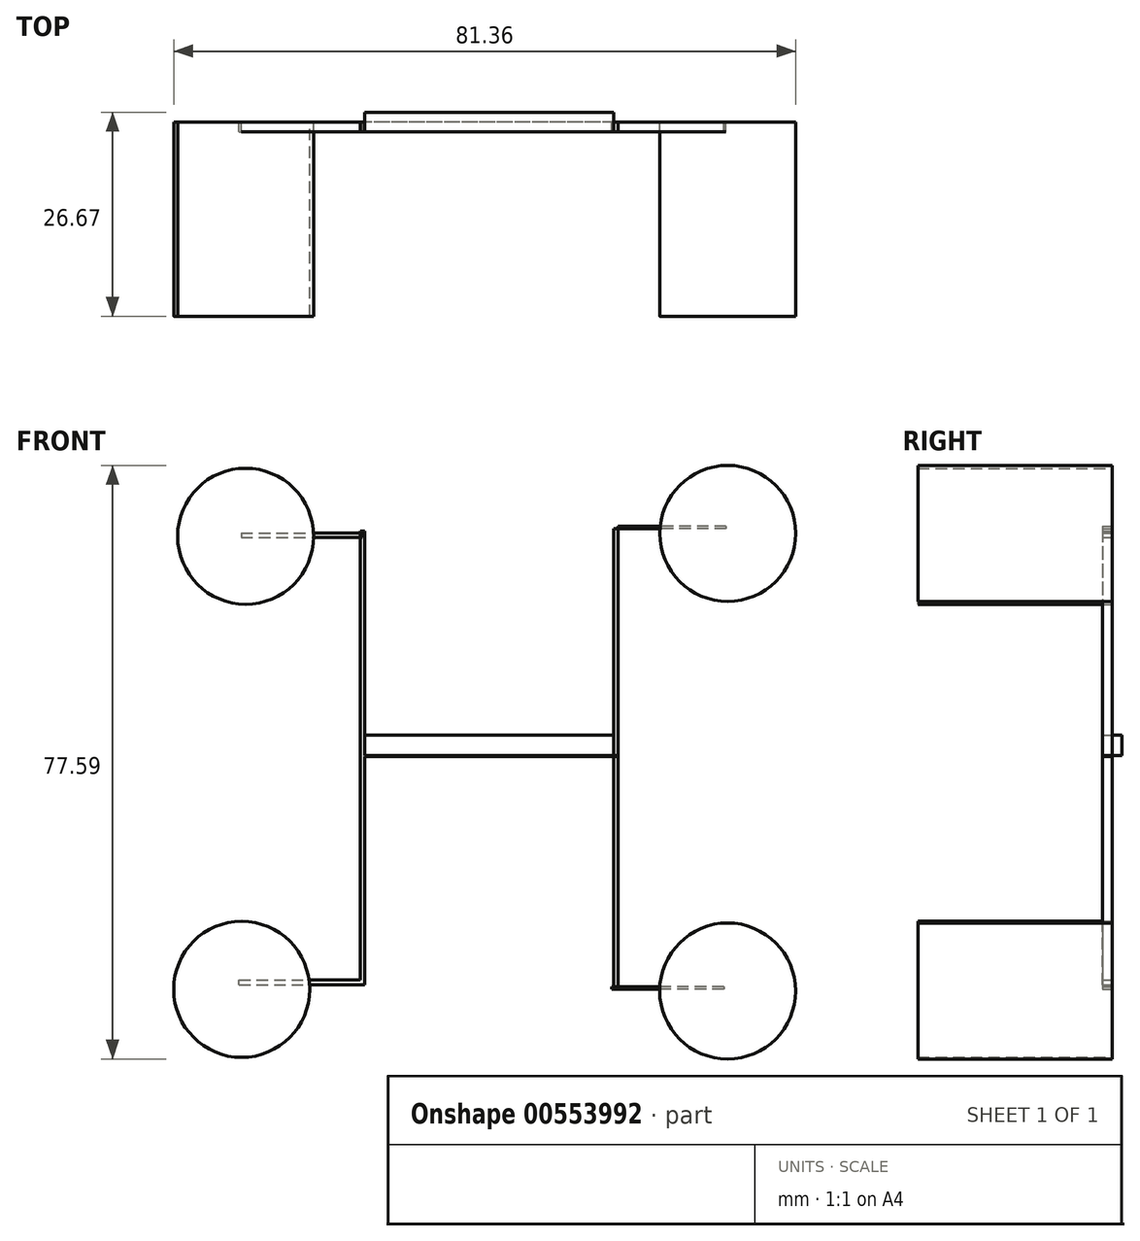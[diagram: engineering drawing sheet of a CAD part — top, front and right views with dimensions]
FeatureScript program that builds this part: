
annotation { "Feature Type Name" : "Feature", "Feature Type Description" : "" }
export const myFeature = defineFeature(function(context is Context, id is Id, definition is map)
    precondition{}
    {
        {
            var Q0;
            Q0=qCreatedBy(makeId("Front.planeOp"),FACE);
            var sketch = newSketch(context, id + "F0", { "sketchPlane" : qUnion([Q0])});
            skCircle(sketch, "E0", {"center": v(-44.94, 47.6) * mm, "radius": 8.9 * mm});
            skCircle(sketch, "E1", {"center": v(18.13, 47.97) * mm, "radius": 8.9 * mm});
            skCircle(sketch, "E2", {"center": v(-45.45, -11.64) * mm, "radius": 8.9 * mm});
            skCircle(sketch, "E3", {"center": v(18.12, -11.84) * mm, "radius": 8.9 * mm});
            skLineSegment(sketch, "E4.bottom", {"start": v(18.13, 47.97) * mm, "end": v(18.12, 47.97) * mm});
            skLineSegment(sketch, "E4.top", {"start": v(18.13, -11.84) * mm, "end": v(18.12, -11.84) * mm});
            skLineSegment(sketch, "E5.bottom", {"start": v(-44.94, 47.6) * mm, "end": v(-45.45, 47.6) * mm});
            skLineSegment(sketch, "E5.top", {"start": v(-44.94, -11.64) * mm, "end": v(-45.45, -11.64) * mm});
            skSolve(sketch);
        }
        {
            var Q0;
            Q0 = qSketchRegion(id + "F0", true);
            extrude(context, id + "F1", {"entities" : qUnion([Q0]), "depth" : 25.4 * mm, "offsetDistance" : 25.4 * mm});
        }
        {
            var Q0;
            Q0=qCreatedBy(makeId("Front.planeOp"),FACE);
            var sketch = newSketch(context, id + "F2", { "sketchPlane" : qUnion([Q0])});
            skLineSegment(sketch, "E6.bottom", {"start": v(-45.51, 48.3) * mm, "end": v(-29.95, 48.3) * mm});
            skLineSegment(sketch, "E6.top", {"start": v(-45.51, 48.3) * mm, "end": v(-29.95, 48.3) * mm});
            skLineSegment(sketch, "E6.left", {"start": v(-45.51, 48.3) * mm, "end": v(-45.51, 48.3) * mm});
            skLineSegment(sketch, "E6.right", {"start": v(-29.95, 48.3) * mm, "end": v(-29.95, 48.3) * mm});
            skLineSegment(sketch, "E7.bottom", {"start": v(-45.8, -11.01) * mm, "end": v(-29.36, -11.01) * mm});
            skLineSegment(sketch, "E7.top", {"start": v(-45.8, -10.42) * mm, "end": v(-29.36, -10.42) * mm});
            skLineSegment(sketch, "E7.left", {"start": v(-45.8, -11.01) * mm, "end": v(-45.8, -10.42) * mm});
            skLineSegment(sketch, "E7.right", {"start": v(-29.36, -11.01) * mm, "end": v(-29.36, -10.42) * mm});
            skLineSegment(sketch, "E8.bottom", {"start": v(17.62, -11.3) * mm, "end": v(2.94, -11.3) * mm});
            skLineSegment(sketch, "E8.top", {"start": v(17.62, -11.6) * mm, "end": v(2.94, -11.6) * mm});
            skLineSegment(sketch, "E8.left", {"start": v(17.62, -11.3) * mm, "end": v(17.62, -11.6) * mm});
            skLineSegment(sketch, "E8.right", {"start": v(2.94, -11.3) * mm, "end": v(2.94, -11.6) * mm});
            skLineSegment(sketch, "E9.bottom", {"start": v(17.91, 48.89) * mm, "end": v(3.82, 48.89) * mm});
            skLineSegment(sketch, "E9.top", {"start": v(17.91, 48.6) * mm, "end": v(3.82, 48.6) * mm});
            skLineSegment(sketch, "E9.left", {"start": v(17.91, 48.89) * mm, "end": v(17.91, 48.6) * mm});
            skLineSegment(sketch, "E9.right", {"start": v(3.82, 48.89) * mm, "end": v(3.82, 48.6) * mm});
            skLineSegment(sketch, "E10.bottom", {"start": v(3.82, 48.6) * mm, "end": v(2.94, 48.6) * mm});
            skLineSegment(sketch, "E10.top", {"start": v(3.82, -11.3) * mm, "end": v(2.94, -11.3) * mm});
            skLineSegment(sketch, "E11.bottom", {"start": v(-29.95, 48.3) * mm, "end": v(-29.36, 48.3) * mm});
            skLineSegment(sketch, "E11.top", {"start": v(-29.95, -10.42) * mm, "end": v(-29.36, -10.42) * mm});
            skLineSegment(sketch, "E11.left", {"start": v(-29.95, 48.3) * mm, "end": v(-29.95, -10.42) * mm});
            skLineSegment(sketch, "E11.right", {"start": v(-29.36, 48.3) * mm, "end": v(-29.36, -10.42) * mm});
            skLineSegment(sketch, "E12.bottom", {"start": v(3.82, 48.89) * mm, "end": v(3.82, 48.89) * mm});
            skLineSegment(sketch, "E12.top", {"start": v(3.82, -11.3) * mm, "end": v(3.82, -11.3) * mm});
            skLineSegment(sketch, "E12.left", {"start": v(3.82, 48.89) * mm, "end": v(3.82, -11.3) * mm});
            skLineSegment(sketch, "E12.right", {"start": v(3.82, 48.89) * mm, "end": v(3.82, -11.3) * mm});
            skLineSegment(sketch, "E13.bottom", {"start": v(3.82, 18.8) * mm, "end": v(-29.36, 18.8) * mm});
            skLineSegment(sketch, "E13.top", {"start": v(3.82, 18.94) * mm, "end": v(-29.36, 18.94) * mm});
            skLineSegment(sketch, "E13.left", {"start": v(3.82, 18.8) * mm, "end": v(3.82, 18.94) * mm});
            skLineSegment(sketch, "E13.right", {"start": v(-29.36, 18.8) * mm, "end": v(-29.36, 18.94) * mm});
            skSolve(sketch);
        }
        {
            var Q0;
            Q0 = qSketchRegion(id + "F2", true);
            extrude(context, id + "F3", {"entities" : qUnion([Q0]), "depth" : 1.27 * mm, "offsetDistance" : 25.4 * mm});
        }
        {
            var Q0;
            Q0=qCreatedBy(makeId("Front.planeOp"),FACE);
            var sketch = newSketch(context, id + "F4", { "sketchPlane" : qUnion([Q0])});
            skLineSegment(sketch, "E14.bottom", {"start": v(-45.51, 48) * mm, "end": v(-29.66, 48) * mm});
            skLineSegment(sketch, "E14.top", {"start": v(-45.51, 47.42) * mm, "end": v(-29.66, 47.42) * mm});
            skLineSegment(sketch, "E14.left", {"start": v(-45.51, 48) * mm, "end": v(-45.51, 47.42) * mm});
            skLineSegment(sketch, "E14.right", {"start": v(-29.66, 48) * mm, "end": v(-29.66, 47.42) * mm});
            skLineSegment(sketch, "E15.bottom", {"start": v(3.82, 48.6) * mm, "end": v(3.23, 48.6) * mm});
            skLineSegment(sketch, "E15.top", {"start": v(3.82, -11.3) * mm, "end": v(3.23, -11.3) * mm});
            skLineSegment(sketch, "E15.left", {"start": v(3.82, 48.6) * mm, "end": v(3.82, -11.3) * mm});
            skLineSegment(sketch, "E15.right", {"start": v(3.23, 48.6) * mm, "end": v(3.23, -11.3) * mm});
            skSolve(sketch);
        }
        {
            var Q0;
            Q0 = qSketchRegion(id + "F4", true);
            extrude(context, id + "F5", {"entities" : qUnion([Q0]), "depth" : 1.27 * mm, "offsetDistance" : 25.4 * mm});
        }
        {
            var Q0;
            Q0=qCreatedBy(makeId("Front.planeOp"),FACE);
            var sketch = newSketch(context, id + "F6", { "sketchPlane" : qUnion([Q0])});
            skLineSegment(sketch, "E16.left", {"start": v(-29.36, 18.64) * mm, "end": v(-29.36, 18.94) * mm});
            skLineSegment(sketch, "E16.right", {"start": v(3.23, 18.64) * mm, "end": v(3.23, 18.94) * mm});
            skLineSegment(sketch, "E17.left", {"start": v(-29.36, 18.94) * mm, "end": v(-29.36, 18.94) * mm});
            skLineSegment(sketch, "E17.right", {"start": v(3.23, 18.94) * mm, "end": v(3.23, 18.94) * mm});
            skLineSegment(sketch, "E18.bottom", {"start": v(-29.36, 18.94) * mm, "end": v(3.23, 18.94) * mm});
            skLineSegment(sketch, "E18.top", {"start": v(-29.36, 21.58) * mm, "end": v(3.23, 21.58) * mm});
            skLineSegment(sketch, "E18.left", {"start": v(-29.36, 18.94) * mm, "end": v(-29.36, 21.58) * mm});
            skLineSegment(sketch, "E18.right", {"start": v(3.23, 18.94) * mm, "end": v(3.23, 21.58) * mm});
            skSolve(sketch);
        }
        {
            var Q0;
            Q0 = qSketchRegion(id + "F6", true);
            extrude(context, id + "F7", {"entities" : qUnion([Q0]), "depth" : 1.27 * mm, "offsetDistance" : 25.4 * mm, "hasSecondDirection" : true, "secondDirectionOppositeDirection" : true, "secondDirectionDepth" : 1.27 * mm});
        }
    });
